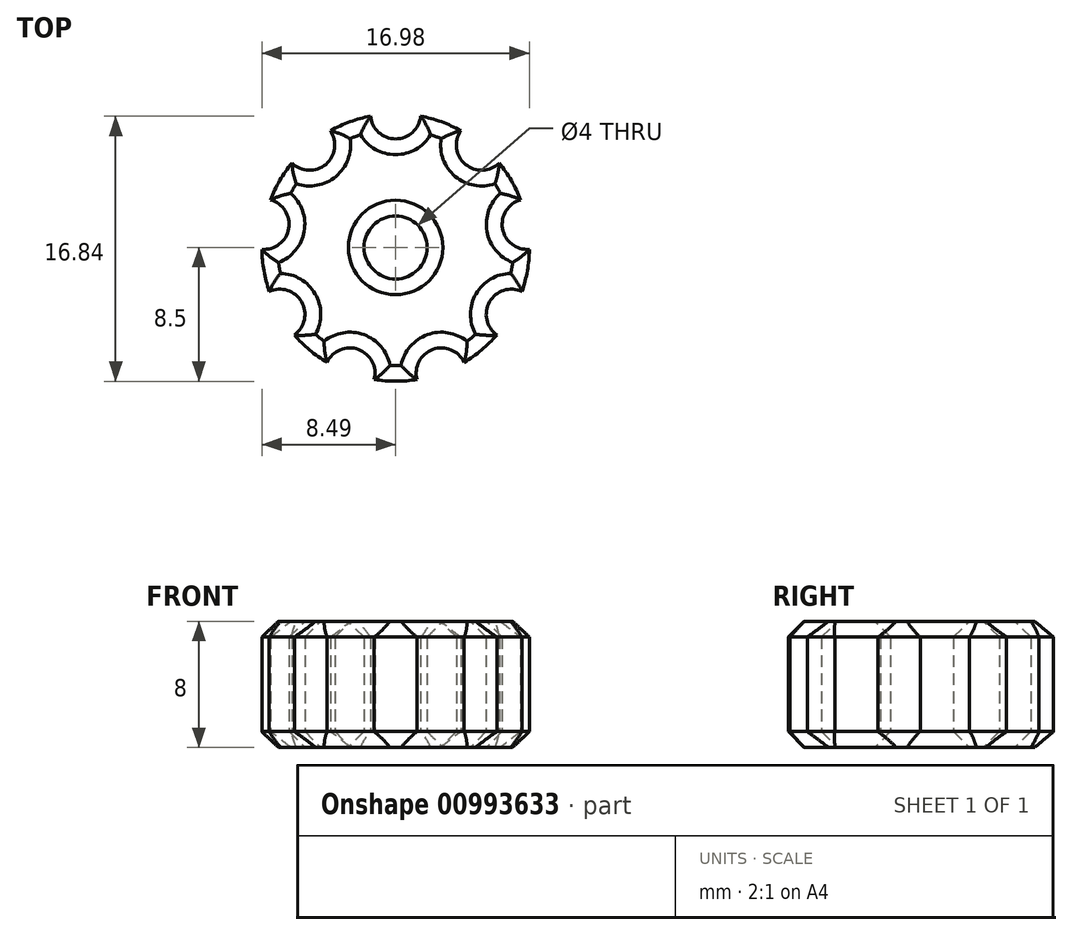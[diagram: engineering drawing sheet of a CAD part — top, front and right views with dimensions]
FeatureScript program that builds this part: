
annotation { "Feature Type Name" : "Feature", "Feature Type Description" : "" }
export const myFeature = defineFeature(function(context is Context, id is Id, definition is map)
    precondition{}
    {
        {
            var Q0;
            Q0=qCreatedBy(makeId("Top.planeOp"),FACE);
            var sketch = newSketch(context, id + "F0", { "sketchPlane" : qUnion([Q0])});
            skCircle(sketch, "E0", {"center": v(0, 0) * mm, "radius": 2 * mm});
            skCircle(sketch, "E1", {"center": v(0, 0) * mm, "radius": 8.5 * mm});
            skCircle(sketch, "E2", {"center": v(0, 8.5) * mm, "radius": 1.6 * mm});
            skCircle(sketch, "E3.1.0", {"center": v(-5.46, 6.5) * mm, "radius": 1.6 * mm});
            skCircle(sketch, "E3.2.0", {"center": v(-8.37, 1.48) * mm, "radius": 1.6 * mm});
            skCircle(sketch, "E4.1.3.0", {"center": v(-7.36, -4.25) * mm, "radius": 1.6 * mm});
            skCircle(sketch, "E5.1.4.0", {"center": v(-2.9, -7.98) * mm, "radius": 1.6 * mm});
            skCircle(sketch, "E5.1.5.0", {"center": v(2.9, -7.98) * mm, "radius": 1.6 * mm});
            skCircle(sketch, "E5.1.6.0", {"center": v(7.36, -4.25) * mm, "radius": 1.6 * mm});
            skCircle(sketch, "E5.1.7.0", {"center": v(8.37, 1.48) * mm, "radius": 1.6 * mm});
            skPoint(sketch, "E6", {"position": v(1.6, 8.34) * mm});
            skPoint(sketch, "E7", {"position": v(4.14, 7.42) * mm});
            skCircle(sketch, "E8.1.8.0", {"center": v(5.46, 6.5) * mm, "radius": 1.6 * mm});
            skSolve(sketch);
        }
        {
            var Q0;
            Q0=makeQuery(id+"F0.imprint","IMPRINT",FACE,{"disambiguationData":[TD([[makeQuery(id+"F0.imprint","IMPRINT",EDGE,{"derivedFrom":sQuery(id+"F0.wireOp",EDGE,"E0")}),-1.0]])]});
            extrude(context, id + "F1", {"entities" : qUnion([Q0]), "depth" : 8 * mm, "offsetDistance" : 25 * mm});
        }
        {
            var Q0;
            Q0=makeQuery(id+"F1.opExtrude","CAP_FACE",FACE,{"disambiguationData":[OSD([sQuery(id+"F0.wireOp",EDGE,"E0"),sQuery(id+"F0.wireOp",EDGE,"E1"),sQuery(id+"F0.wireOp",EDGE,"E2"),sQuery(id+"F0.wireOp",EDGE,"E3.1.0"),sQuery(id+"F0.wireOp",EDGE,"E3.2.0"),sQuery(id+"F0.wireOp",EDGE,"E4.1.3.0"),sQuery(id+"F0.wireOp",EDGE,"E5.1.4.0"),sQuery(id+"F0.wireOp",EDGE,"E5.1.5.0"),sQuery(id+"F0.wireOp",EDGE,"E5.1.6.0"),sQuery(id+"F0.wireOp",EDGE,"E5.1.7.0")])],"isStart":false});
            var Q1;
            Q1=makeQuery(id+"F1.opExtrude","CAP_FACE",FACE,{"disambiguationData":[OSD([sQuery(id+"F0.wireOp",EDGE,"E0"),sQuery(id+"F0.wireOp",EDGE,"E1"),sQuery(id+"F0.wireOp",EDGE,"E2"),sQuery(id+"F0.wireOp",EDGE,"E3.1.0"),sQuery(id+"F0.wireOp",EDGE,"E3.2.0"),sQuery(id+"F0.wireOp",EDGE,"E4.1.3.0"),sQuery(id+"F0.wireOp",EDGE,"E5.1.4.0"),sQuery(id+"F0.wireOp",EDGE,"E5.1.5.0"),sQuery(id+"F0.wireOp",EDGE,"E5.1.6.0"),sQuery(id+"F0.wireOp",EDGE,"E5.1.7.0")])],"isStart":true});
            chamfer(context, id + "F2", {"entities" : qUnion([Q0, Q1]), "width" : 1 * mm, "tangentPropagation" : true});
        }
    });
